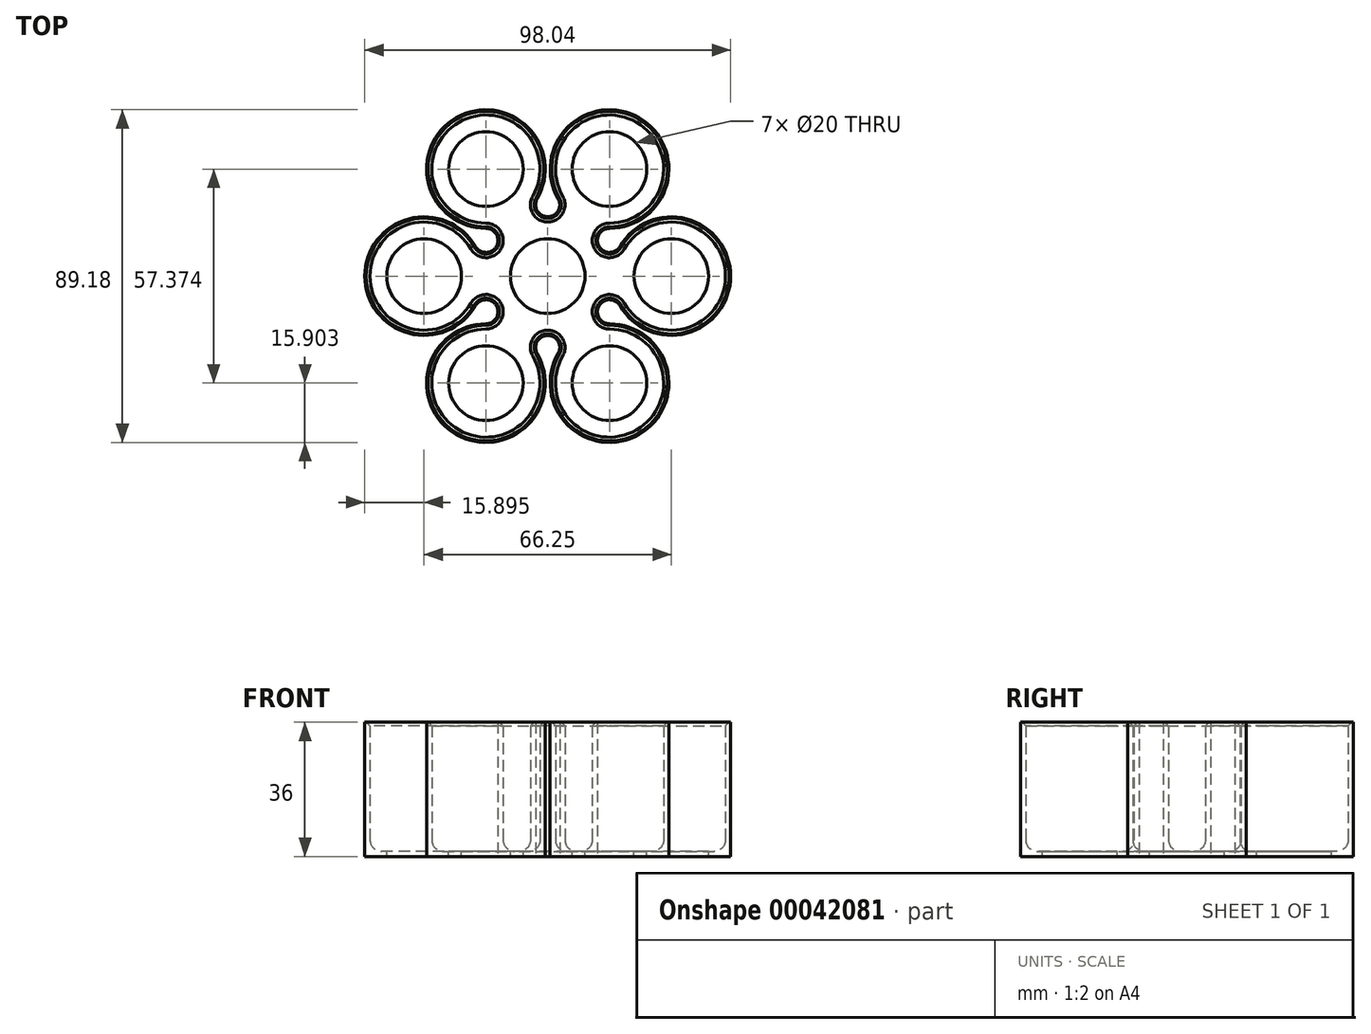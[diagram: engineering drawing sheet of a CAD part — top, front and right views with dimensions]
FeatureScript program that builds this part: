
annotation { "Feature Type Name" : "Feature", "Feature Type Description" : "" }
export const myFeature = defineFeature(function(context is Context, id is Id, definition is map)
    precondition{}
    {
        {
            var Q0;
            Q0=qCreatedBy(makeId("Top.planeOp"),FACE);
            var sketch = newSketch(context, id + "F0", { "sketchPlane" : qUnion([Q0])});
            skPoint(sketch, "E0.0.midPoint", {"position": v(17.67, 0) * mm});
            skLineSegment(sketch, "E1", {"start": v(0, 0) * mm, "end": v(-72.1, 0) * mm, "construction": true});
            skArc(sketch, "E2", {"start": v(-19.36, 7.95) * mm, "mid": v(-49.02, 0) * mm, "end": v(-19.36, -7.95) * mm});
            skArc(sketch, "E3.1.0", {"start": v(-16.56, -12.79) * mm, "mid": v(-24.51, -42.46) * mm, "end": v(-2.8, -20.74) * mm});
            skArc(sketch, "E3.2.0", {"start": v(2.8, -20.74) * mm, "mid": v(24.51, -42.46) * mm, "end": v(16.56, -12.79) * mm});
            skArc(sketch, "E3.3.0", {"start": v(19.36, -7.95) * mm, "mid": v(49.02, 0) * mm, "end": v(19.36, 7.95) * mm});
            skArc(sketch, "E3.4.0", {"start": v(16.56, 12.79) * mm, "mid": v(24.51, 42.46) * mm, "end": v(2.8, 20.74) * mm});
            skArc(sketch, "E3.5.0", {"start": v(-2.8, 20.74) * mm, "mid": v(-24.51, 42.46) * mm, "end": v(-16.56, 12.79) * mm});
            skPoint(sketch, "E3.center", {"position": v(0, 0) * mm});
            skLineSegment(sketch, "E4", {"start": v(0, 0) * mm, "end": v(-16.56, 28.69) * mm, "construction": true});
            skLineSegment(sketch, "E5", {"start": v(16.56, 28.69) * mm, "end": v(0, 0) * mm, "construction": true});
            skLineSegment(sketch, "E6", {"start": v(-16.56, 28.69) * mm, "end": v(16.56, 28.69) * mm, "construction": true});
            skLineSegment(sketch, "E7", {"start": v(16.56, 28.69) * mm, "end": v(-8.28, 14.34) * mm, "construction": true});
            skLineSegment(sketch, "E8", {"start": v(0, 0) * mm, "end": v(0, 28.69) * mm, "construction": true});
            skArc(sketch, "E9", {"start": v(-2.8, 20.74) * mm, "mid": v(0, 15.9) * mm, "end": v(2.8, 20.74) * mm});
            skArc(sketch, "E10.1.0", {"start": v(-19.36, 7.95) * mm, "mid": v(-13.77, 7.95) * mm, "end": v(-16.56, 12.79) * mm});
            skArc(sketch, "E10.2.0", {"start": v(-16.56, -12.79) * mm, "mid": v(-13.77, -7.95) * mm, "end": v(-19.36, -7.95) * mm});
            skArc(sketch, "E10.3.0", {"start": v(2.8, -20.74) * mm, "mid": v(0, -15.9) * mm, "end": v(-2.8, -20.74) * mm});
            skArc(sketch, "E10.4.0", {"start": v(19.36, -7.95) * mm, "mid": v(13.77, -7.95) * mm, "end": v(16.56, -12.79) * mm});
            skArc(sketch, "E10.5.0", {"start": v(16.56, 12.79) * mm, "mid": v(13.77, 7.95) * mm, "end": v(19.36, 7.95) * mm});
            skCircle(sketch, "E11", {"center": v(-33.12, 0) * mm, "radius": 10 * mm});
            skCircle(sketch, "E12.1.0", {"center": v(-16.56, -28.69) * mm, "radius": 10 * mm});
            skCircle(sketch, "E12.2.0", {"center": v(16.56, -28.69) * mm, "radius": 10 * mm});
            skCircle(sketch, "E12.3.0", {"center": v(33.12, 0) * mm, "radius": 10 * mm});
            skCircle(sketch, "E12.4.0", {"center": v(16.56, 28.69) * mm, "radius": 10 * mm});
            skCircle(sketch, "E12.5.0", {"center": v(-16.56, 28.69) * mm, "radius": 10 * mm});
            skCircle(sketch, "E13", {"center": v(0, 0) * mm, "radius": 10 * mm});
            skSolve(sketch);
        }
        {
            var Q0;
            Q0=makeQuery(id+"F0.imprint","IMPRINT",FACE,{"disambiguationData":[TD([[makeQuery(id+"F0.imprint","IMPRINT",EDGE,{"derivedFrom":sQuery(id+"F0.wireOp",EDGE,"E2")}),1.0]])]});
            var Q1;
            Q1=makeQuery(id+"F0.imprint","IMPRINT",FACE,{"disambiguationData":[TD([[makeQuery(id+"F0.imprint","IMPRINT",EDGE,{"derivedFrom":sQuery(id+"F0.wireOp",EDGE,"E12.4.0")}),1.0]])]});
            var Q2;
            Q2=makeQuery(id+"F0.imprint","IMPRINT",FACE,{"disambiguationData":[TD([[makeQuery(id+"F0.imprint","IMPRINT",EDGE,{"derivedFrom":sQuery(id+"F0.wireOp",EDGE,"E12.3.0")}),1.0]])]});
            var Q3;
            Q3=makeQuery(id+"F0.imprint","IMPRINT",FACE,{"disambiguationData":[TD([[makeQuery(id+"F0.imprint","IMPRINT",EDGE,{"derivedFrom":sQuery(id+"F0.wireOp",EDGE,"E12.2.0")}),1.0]])]});
            var Q4;
            Q4=makeQuery(id+"F0.imprint","IMPRINT",FACE,{"disambiguationData":[TD([[makeQuery(id+"F0.imprint","IMPRINT",EDGE,{"derivedFrom":sQuery(id+"F0.wireOp",EDGE,"E12.1.0")}),1.0]])]});
            var Q5;
            Q5=makeQuery(id+"F0.imprint","IMPRINT",FACE,{"disambiguationData":[TD([[makeQuery(id+"F0.imprint","IMPRINT",EDGE,{"derivedFrom":sQuery(id+"F0.wireOp",EDGE,"E11")}),1.0]])]});
            var Q6;
            Q6=makeQuery(id+"F0.imprint","IMPRINT",FACE,{"disambiguationData":[TD([[makeQuery(id+"F0.imprint","IMPRINT",EDGE,{"derivedFrom":sQuery(id+"F0.wireOp",EDGE,"E12.5.0")}),1.0]])]});
            var Q7;
            Q7=makeQuery(id+"F0.imprint","IMPRINT",FACE,{"disambiguationData":[TD([[makeQuery(id+"F0.imprint","IMPRINT",EDGE,{"derivedFrom":sQuery(id+"F0.wireOp",EDGE,"E13")}),1.0]])]});
            extrude(context, id + "F1", {"entities" : qUnion([Q0, Q1, Q2, Q3, Q4, Q5, Q6, Q7]), "depth" : 36 * mm});
        }
        {
            var Q0;
            Q0=makeQuery(id+"F1.opExtrude","CAP_FACE",FACE,{"disambiguationData":[OSD([sQuery(id+"F0.wireOp",EDGE,"E2"),sQuery(id+"F0.wireOp",EDGE,"E3.1.0"),sQuery(id+"F0.wireOp",EDGE,"E3.2.0"),sQuery(id+"F0.wireOp",EDGE,"E3.3.0"),sQuery(id+"F0.wireOp",EDGE,"E3.4.0"),sQuery(id+"F0.wireOp",EDGE,"E3.5.0"),sQuery(id+"F0.wireOp",EDGE,"E9"),sQuery(id+"F0.wireOp",EDGE,"E10.1.0"),sQuery(id+"F0.wireOp",EDGE,"E10.2.0"),sQuery(id+"F0.wireOp",EDGE,"E10.3.0"),sQuery(id+"F0.wireOp",EDGE,"E10.4.0"),sQuery(id+"F0.wireOp",EDGE,"E10.5.0")])],"isStart":false});
            shell(context, id + "F2", {"entities" : qUnion([Q0]), "thickness" : 1.4 * mm});
        }
        {
            var Q0;
            Q0=makeQuery(id+"F0.imprint","IMPRINT",FACE,{"disambiguationData":[TD([[makeQuery(id+"F0.imprint","IMPRINT",EDGE,{"derivedFrom":sQuery(id+"F0.wireOp",EDGE,"E11")}),1.0]])]});
            var Q1;
            Q1=makeQuery(id+"F0.imprint","IMPRINT",FACE,{"disambiguationData":[TD([[makeQuery(id+"F0.imprint","IMPRINT",EDGE,{"derivedFrom":sQuery(id+"F0.wireOp",EDGE,"E12.1.0")}),1.0]])]});
            var Q2;
            Q2=makeQuery(id+"F0.imprint","IMPRINT",FACE,{"disambiguationData":[TD([[makeQuery(id+"F0.imprint","IMPRINT",EDGE,{"derivedFrom":sQuery(id+"F0.wireOp",EDGE,"E12.2.0")}),1.0]])]});
            var Q3;
            Q3=makeQuery(id+"F0.imprint","IMPRINT",FACE,{"disambiguationData":[TD([[makeQuery(id+"F0.imprint","IMPRINT",EDGE,{"derivedFrom":sQuery(id+"F0.wireOp",EDGE,"E12.3.0")}),1.0]])]});
            var Q4;
            Q4=makeQuery(id+"F0.imprint","IMPRINT",FACE,{"disambiguationData":[TD([[makeQuery(id+"F0.imprint","IMPRINT",EDGE,{"derivedFrom":sQuery(id+"F0.wireOp",EDGE,"E12.4.0")}),1.0]])]});
            var Q5;
            Q5=makeQuery(id+"F0.imprint","IMPRINT",FACE,{"disambiguationData":[TD([[makeQuery(id+"F0.imprint","IMPRINT",EDGE,{"derivedFrom":sQuery(id+"F0.wireOp",EDGE,"E12.5.0")}),1.0]])]});
            var Q6;
            Q6=makeQuery(id+"F0.imprint","IMPRINT",FACE,{"disambiguationData":[TD([[makeQuery(id+"F0.imprint","IMPRINT",EDGE,{"derivedFrom":sQuery(id+"F0.wireOp",EDGE,"E13")}),1.0]])]});
            var Q7;
            Q7=sQuery(id+"F0.wireOp",EDGE,"E11");
            var Q8;
            Q8=sQuery(id+"F0.wireOp",EDGE,"E12.5.0");
            var Q9;
            Q9=sQuery(id+"F0.wireOp",EDGE,"E12.4.0");
            var Q10;
            Q10=sQuery(id+"F0.wireOp",EDGE,"E12.3.0");
            var Q11;
            Q11=sQuery(id+"F0.wireOp",EDGE,"E12.2.0");
            var Q12;
            Q12=sQuery(id+"F0.wireOp",EDGE,"E12.1.0");
            extrude(context, id + "F3", {"entities" : qUnion([Q0, Q1, Q2, Q3, Q4, Q5, Q6]), "surfaceEntities" : qUnion([Q7, Q8, Q9, Q10, Q11, Q12]), "endBound" : BoundingType.SYMMETRIC, "oppositeDirection" : true, "depth" : 25 * mm});
        }
        {
            var Q0;
            Q0=makeQuery(id+"F3.opExtrude","SWEPT_BODY",BODY,{"disambiguationData":[OSD([sQuery(id+"F0.wireOp",EDGE,"E12.3.0")])]});
            var Q1;
            Q1=makeQuery(id+"F3.opExtrude","SWEPT_BODY",BODY,{"disambiguationData":[OSD([sQuery(id+"F0.wireOp",EDGE,"E12.2.0")])]});
            var Q2;
            Q2=makeQuery(id+"F3.opExtrude","SWEPT_BODY",BODY,{"disambiguationData":[OSD([sQuery(id+"F0.wireOp",EDGE,"E13")])]});
            var Q3;
            Q3=makeQuery(id+"F3.opExtrude","SWEPT_BODY",BODY,{"disambiguationData":[OSD([sQuery(id+"F0.wireOp",EDGE,"E11")])]});
            var Q4;
            Q4=makeQuery(id+"F3.opExtrude","SWEPT_BODY",BODY,{"disambiguationData":[OSD([sQuery(id+"F0.wireOp",EDGE,"E12.5.0")])]});
            var Q5;
            Q5=makeQuery(id+"F3.opExtrude","SWEPT_BODY",BODY,{"disambiguationData":[OSD([sQuery(id+"F0.wireOp",EDGE,"E12.4.0")])]});
            var Q6;
            Q6=makeQuery(id+"F3.opExtrude","SWEPT_BODY",BODY,{"disambiguationData":[OSD([sQuery(id+"F0.wireOp",EDGE,"E12.1.0")])]});
            var Q7;
            Q7=makeQuery(id+"F1.opExtrude","SWEPT_BODY",BODY,{"disambiguationData":[OSD([sQuery(id+"F0.wireOp",EDGE,"E2"),sQuery(id+"F0.wireOp",EDGE,"E3.1.0"),sQuery(id+"F0.wireOp",EDGE,"E3.2.0"),sQuery(id+"F0.wireOp",EDGE,"E3.3.0"),sQuery(id+"F0.wireOp",EDGE,"E3.4.0"),sQuery(id+"F0.wireOp",EDGE,"E3.5.0"),sQuery(id+"F0.wireOp",EDGE,"E9"),sQuery(id+"F0.wireOp",EDGE,"E10.1.0"),sQuery(id+"F0.wireOp",EDGE,"E10.2.0"),sQuery(id+"F0.wireOp",EDGE,"E10.3.0"),sQuery(id+"F0.wireOp",EDGE,"E10.4.0"),sQuery(id+"F0.wireOp",EDGE,"E10.5.0")])]});
            booleanBodies(context, id + "F4", {"operationType" : BooleanOperationType.SUBTRACTION, "tools" : qUnion([Q0, Q1, Q2, Q3, Q4, Q5, Q6]), "targets" : qUnion([Q7])});
        }
        {
            var Q0;
            {var subQ0=sQuery(id+"F0.wireOp",EDGE,"E3.3.0");Q0=makeQuery(id+"F2.opShell","OFFSET_EDGE",EDGE,{"disambiguationData":[OSD([subQ0]),TDD([makeQuery(id+"F1.opExtrude","CAP_EDGE",EDGE,{"disambiguationData":[OSD([subQ0])],"isStart":false})])]});}
            chamfer(context, id + "F5", {"entities" : qUnion([Q0]), "width" : 1 * mm, "tangentPropagation" : true});
        }
        {
            var Q0;
            {var subQ0=sQuery(id+"F0.wireOp",EDGE,"E3.3.0");Q0=makeQuery(id+"F2.opShell","OFFSET_EDGE",EDGE,{"disambiguationData":[OSD([subQ0]),TDD([makeQuery(id+"F1.opExtrude","CAP_EDGE",EDGE,{"disambiguationData":[OSD([subQ0])],"isStart":true})])]});}
            fillet(context, id + "F6", {"entities" : qUnion([Q0]), "radius" : 3 * mm, "tangentPropagation" : true, "allowEdgeOverflow" : false});
        }
    });
